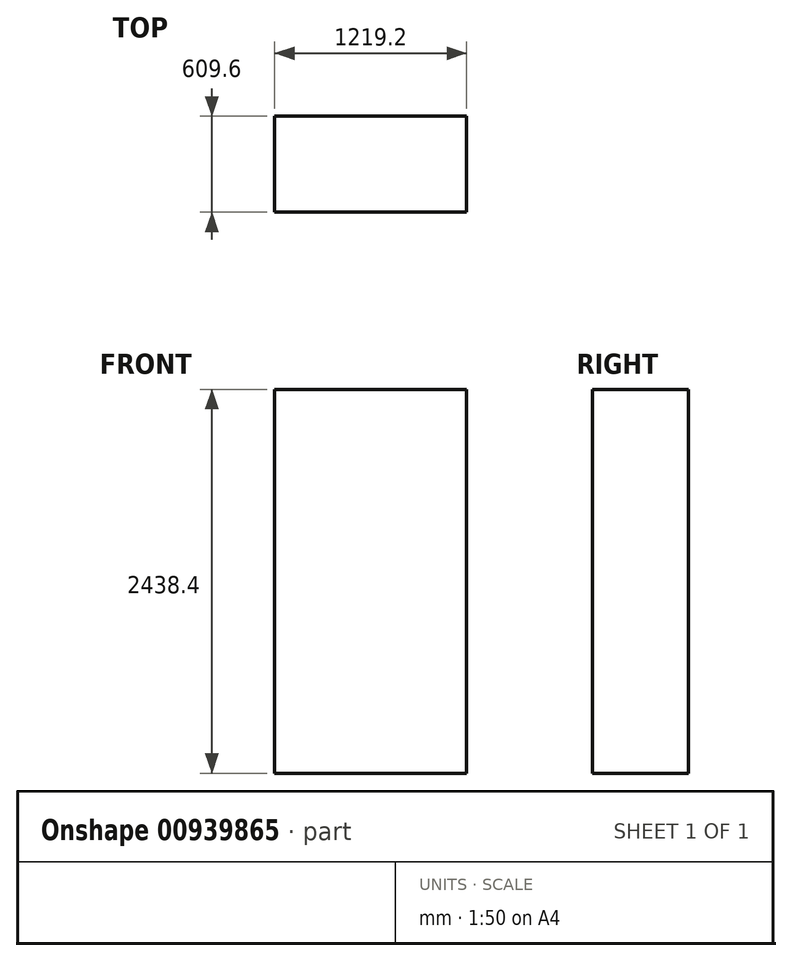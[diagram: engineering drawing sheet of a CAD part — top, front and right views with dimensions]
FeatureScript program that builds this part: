
annotation { "Feature Type Name" : "Feature", "Feature Type Description" : "" }
export const myFeature = defineFeature(function(context is Context, id is Id, definition is map)
    precondition{}
    {
        {
            var Q0;
            Q0=qCreatedBy(makeId("Top.planeOp"),FACE);
            var sketch = newSketch(context, id + "F0", { "sketchPlane" : qUnion([Q0])});
            skLineSegment(sketch, "E0.bottom", {"start": v(609.6, 304.8) * mm, "end": v(-609.6, 304.8) * mm});
            skLineSegment(sketch, "E0.top", {"start": v(609.6, -304.8) * mm, "end": v(-609.6, -304.8) * mm});
            skLineSegment(sketch, "E0.left", {"start": v(609.6, 304.8) * mm, "end": v(609.6, -304.8) * mm});
            skLineSegment(sketch, "E0.right", {"start": v(-609.6, 304.8) * mm, "end": v(-609.6, -304.8) * mm});
            skPoint(sketch, "E0.middle", {"position": v(0, 0) * mm});
            skSolve(sketch);
        }
        {
            var Q0;
            Q0 = qSketchRegion(id + "F0", true);
            extrude(context, id + "F1", {"entities" : qUnion([Q0]), "depth" : 2438.4 * mm, "offsetDistance" : 25.4 * mm});
        }
    });
